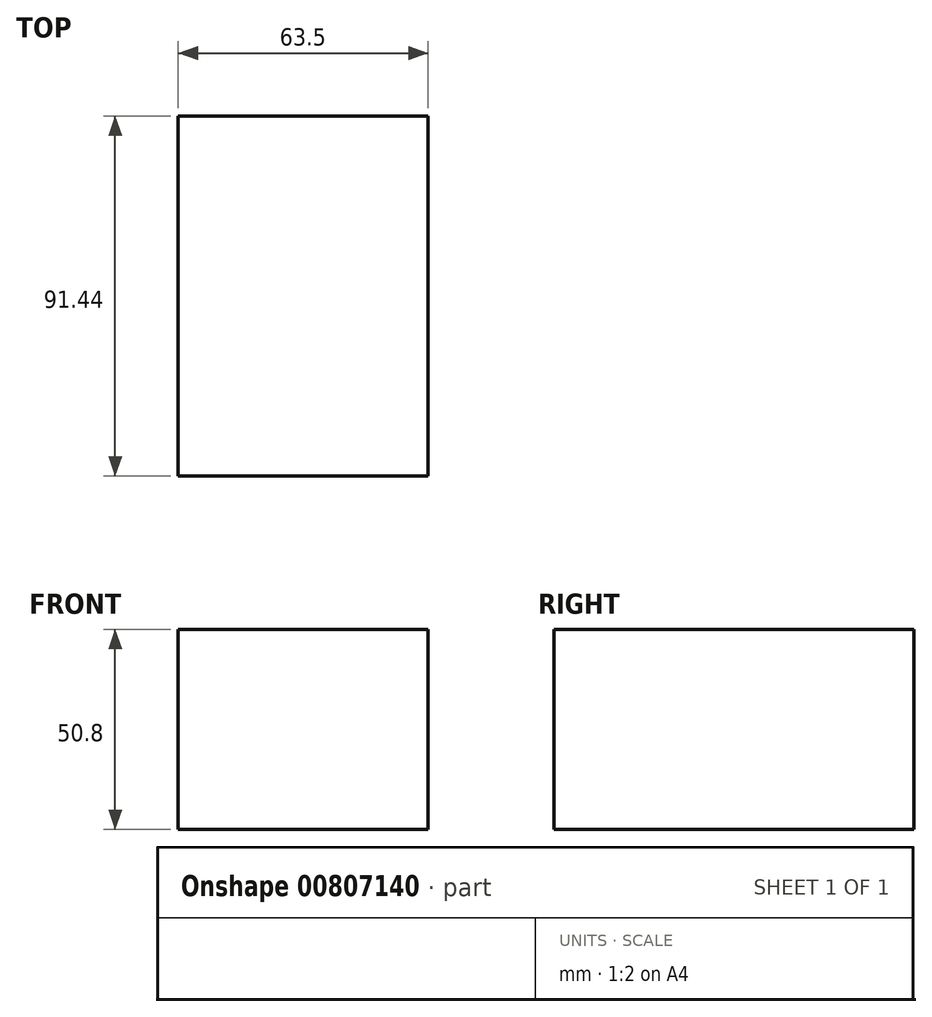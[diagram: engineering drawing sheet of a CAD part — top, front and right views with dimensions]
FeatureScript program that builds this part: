
annotation { "Feature Type Name" : "Feature", "Feature Type Description" : "" }
export const myFeature = defineFeature(function(context is Context, id is Id, definition is map)
    precondition{}
    {
        {
            var Q0;
            Q0=qCreatedBy(makeId("Top.planeOp"),FACE);
            var sketch = newSketch(context, id + "F0", { "sketchPlane" : qUnion([Q0])});
            skLineSegment(sketch, "E0.bottom", {"start": v(0, 0) * mm, "end": v(63.5, 0) * mm});
            skLineSegment(sketch, "E0.top", {"start": v(0, -91.44) * mm, "end": v(63.5, -91.44) * mm});
            skLineSegment(sketch, "E0.left", {"start": v(0, 0) * mm, "end": v(0, -91.44) * mm});
            skLineSegment(sketch, "E0.right", {"start": v(63.5, 0) * mm, "end": v(63.5, -91.44) * mm});
            skSolve(sketch);
        }
        {
            var Q0;
            Q0 = qSketchRegion(id + "F0", true);
            extrude(context, id + "F1", {"entities" : qUnion([Q0]), "depth" : 50.8 * mm, "offsetDistance" : 25.4 * mm});
        }
    });
